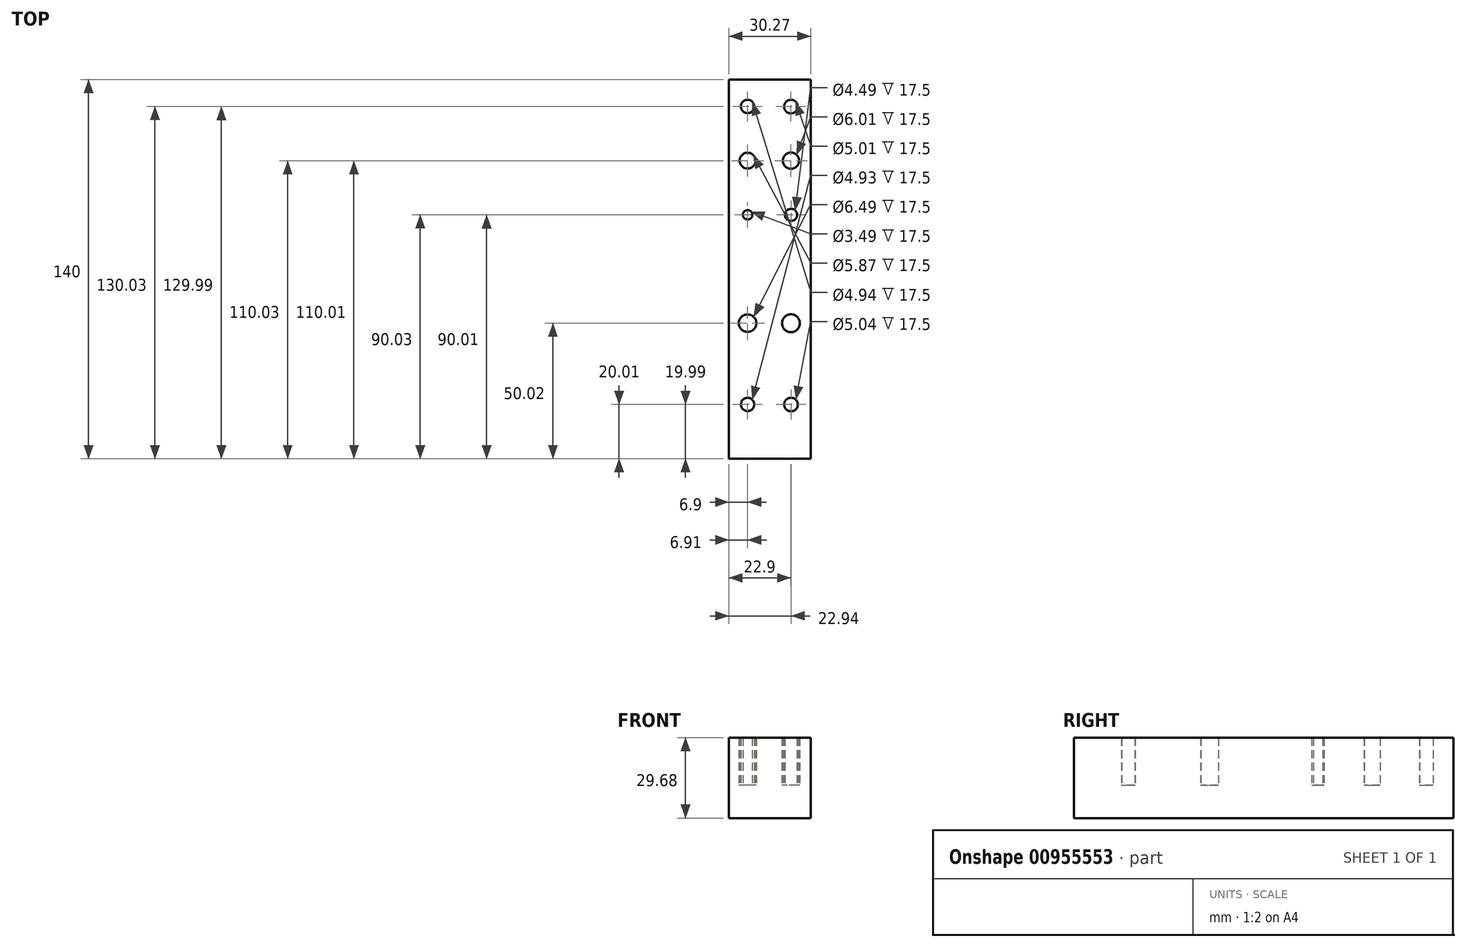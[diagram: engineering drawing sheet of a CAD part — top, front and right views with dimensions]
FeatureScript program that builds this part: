
annotation { "Feature Type Name" : "Feature", "Feature Type Description" : "" }
export const myFeature = defineFeature(function(context is Context, id is Id, definition is map)
    precondition{}
    {
        {
            var Q0;
            Q0=qCreatedBy(makeId("Top.planeOp"),FACE);
            var sketch = newSketch(context, id + "F0", { "sketchPlane" : qUnion([Q0])});
            skLineSegment(sketch, "E0.bottom", {"start": v(30.27, 140) * mm, "end": v(0, 140) * mm});
            skLineSegment(sketch, "E0.top", {"start": v(30.27, 0) * mm, "end": v(0, 0) * mm});
            skLineSegment(sketch, "E0.left", {"start": v(30.27, 140) * mm, "end": v(30.27, 0) * mm});
            skLineSegment(sketch, "E0.right", {"start": v(0, 140) * mm, "end": v(0, 0) * mm});
            skCircle(sketch, "E1", {"center": v(6.9, 130.03) * mm, "radius": 2.47 * mm});
            skCircle(sketch, "E2", {"center": v(6.9, 110.03) * mm, "radius": 2.94 * mm});
            skCircle(sketch, "E3", {"center": v(6.9, 90.03) * mm, "radius": 1.75 * mm});
            skCircle(sketch, "E4", {"center": v(6.9, 50.02) * mm, "radius": 3.24 * mm});
            skCircle(sketch, "E5", {"center": v(6.91, 20.01) * mm, "radius": 2.46 * mm});
            skCircle(sketch, "E6", {"center": v(22.9, 130) * mm, "radius": 2.5 * mm});
            skCircle(sketch, "E7", {"center": v(22.9, 110.01) * mm, "radius": 3 * mm});
            skCircle(sketch, "E8", {"center": v(22.94, 90.01) * mm, "radius": 2.24 * mm});
            skCircle(sketch, "E9", {"center": v(22.91, 50) * mm, "radius": 3.3 * mm});
            skCircle(sketch, "E10", {"center": v(22.94, 20) * mm, "radius": 2.52 * mm});
            skSolve(sketch);
        }
        {
            var Q0;
            Q0=makeQuery(id+"F0.imprint","IMPRINT",FACE,{"disambiguationData":[TD([[makeQuery(id+"F0.imprint","IMPRINT",EDGE,{"derivedFrom":sQuery(id+"F0.wireOp",EDGE,"E0.bottom")}),1.0]])]});
            extrude(context, id + "F1", {"entities" : qUnion([Q0]), "depth" : 17.5 * mm, "offsetDistance" : 25 * mm});
        }
        {
            var Q0;
            Q0=makeQuery(id+"F1.opExtrude","CAP_FACE",FACE,{"disambiguationData":[OSD([sQuery(id+"F0.wireOp",EDGE,"E0.bottom"),sQuery(id+"F0.wireOp",EDGE,"E0.top"),sQuery(id+"F0.wireOp",EDGE,"E0.left"),sQuery(id+"F0.wireOp",EDGE,"E0.right"),sQuery(id+"F0.wireOp",EDGE,"E1"),sQuery(id+"F0.wireOp",EDGE,"E2"),sQuery(id+"F0.wireOp",EDGE,"E3"),sQuery(id+"F0.wireOp",EDGE,"E4"),sQuery(id+"F0.wireOp",EDGE,"E5"),sQuery(id+"F0.wireOp",EDGE,"E6"),sQuery(id+"F0.wireOp",EDGE,"E7"),sQuery(id+"F0.wireOp",EDGE,"E8"),sQuery(id+"F0.wireOp",EDGE,"E9"),sQuery(id+"F0.wireOp",EDGE,"E10")])],"isStart":true});
            var sketch = newSketch(context, id + "F2", { "sketchPlane" : qUnion([Q0])});
            skLineSegment(sketch, "E11.0.0", {"start": v(30.27, 0) * mm, "end": v(0, 0) * mm});
            skLineSegment(sketch, "E11.0.1", {"start": v(0, 0) * mm, "end": v(0, -140) * mm});
            skLineSegment(sketch, "E11.0.2", {"start": v(0, -140) * mm, "end": v(30.27, -140) * mm});
            skLineSegment(sketch, "E11.0.3", {"start": v(30.27, -140) * mm, "end": v(30.27, 0) * mm});
            skSolve(sketch);
        }
        {
            var Q0;
            Q0 = qSketchRegion(id + "F2", true);
            var Q1;
            Q1 = qSketchRegion(id + "F0", true);
            extrude(context, id + "F3", {"entities" : qUnion([Q0, Q1]), "operationType" : NewBodyOperationType.ADD, "depth" : 12.18 * mm, "offsetDistance" : 25 * mm});
        }
    });
